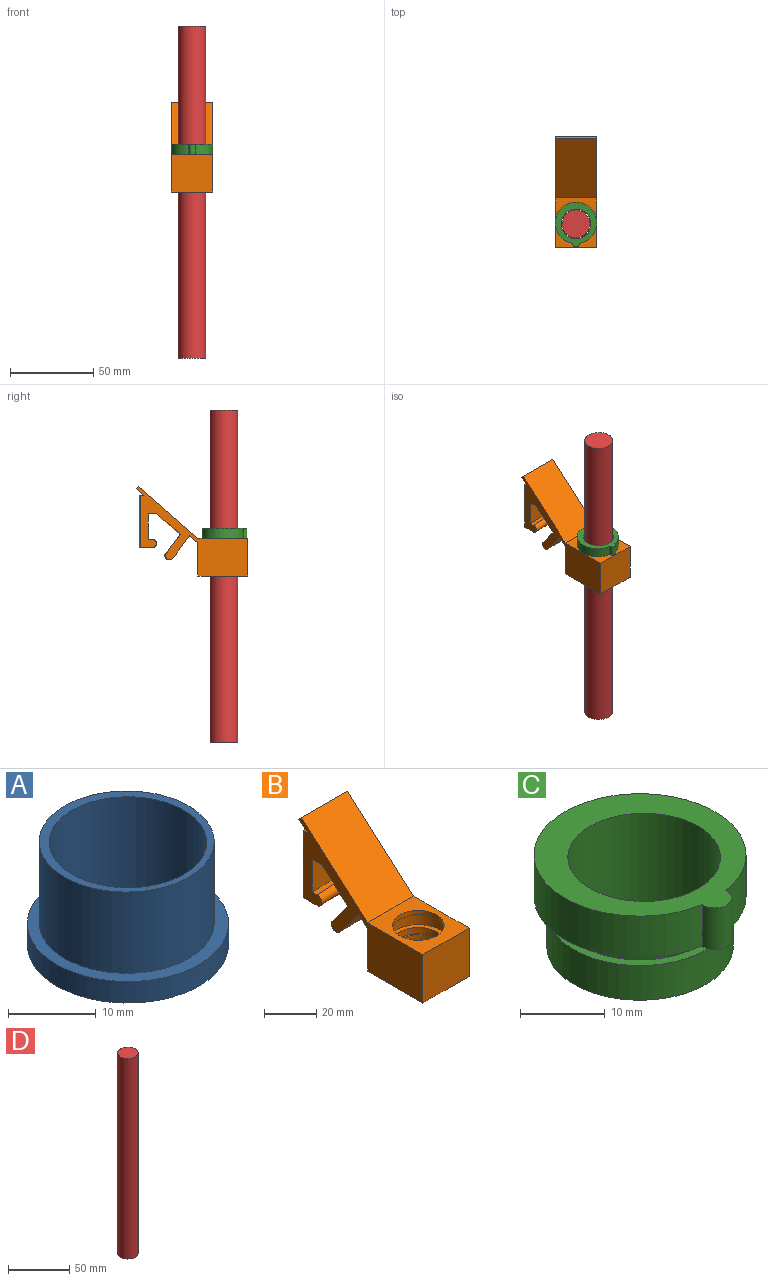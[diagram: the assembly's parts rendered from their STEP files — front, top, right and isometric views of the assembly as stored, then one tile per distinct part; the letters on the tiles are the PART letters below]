
ASSEMBLY  parts=4 mates=2
PART A: 6 faces, bbox 23x23x14.4 mm
  f0: cylinder r=10mm len=20mm, axis (0,0,1), area 713.6mm2, adj f1,f4
  f1: plane 20x20mm, normal (0,0,1), area 59.7mm2, adj f0,f5
  f2: plane 23x23mm, normal (0,0,-1), area 161mm2, adj f3,f5
  f3: cylinder r=11.5mm len=23mm, axis (0,0,1), area 216.8mm2, adj f2,f4
  f4: plane 23x23mm, normal (0,0,1), area 101.3mm2, adj f0,f3
  f5: cylinder r=9mm len=18mm, axis (0,0,-1), area 811.9mm2, adj f1,f2
PART B: 31 faces, bbox 27.2x67.2x54.1 mm
  f0: cylinder r=9.95mm len=19.9mm, axis (0,0,1), area 541.2mm2, adj f26,f28,f29
  f1: plane 67.22x54.07mm, normal (1,0,0), area 1145.6mm2, adj f3,f4,f5,f6,f7,f8,f9,f10
  f2: plane 67.22x54.07mm, normal (-1,0,0), area 1145.6mm2, adj f3,f4,f5,f6,f7,f8,f9,f10
  f3: plane 25x5.21mm, normal (0,0.66,-0.75), area 169.7mm2, adj f1,f2,f15,f20
  f4: plane 35.86x31.37mm, normal (0,-0.66,0.75), area 1191.1mm2, adj f1,f2,f5,f18
  f5: plane 25x1.51mm, normal (0,0.75,0.66), area 50mm2, adj f1,f2,f4,f16
  f6: cylinder r=186.27mm len=31.37mm, axis (0,0,-1), area 784.9mm2, adj f1,f2,f7,f17
  f7: plane 25x7.94mm, normal (0,0,-1), area 187.6mm2, adj f1,f2,f6,f8
  f8: torus R=178.77mm, axis (0,0,-1), area 196.5mm2, adj f1,f2,f7,f9
  f9: plane 25x2.94mm, normal (0,0,1), area 62.6mm2, adj f1,f2,f8,f10
  f10: cylinder r=181.27mm len=25mm, axis (0,0,-1), area 384.7mm2, adj f1,f2,f9,f11
  f11: plane 25x5.44mm, normal (0,0,-1), area 125.1mm2, adj f1,f2,f10,f12
  f12: cone r=162.09mm half-angle=48.8deg, axis (0,0,1), area 472.2mm2, adj f1,f2,f11,f13
  f13: cone r=170.54mm half-angle=36.8deg, axis (0,0,-1), area 353.1mm2, adj f1,f2,f12,f14
  f14: torus R=168.54mm, axis (0,0,-1), area 196.5mm2, adj f1,f2,f13,f15
  f15: cone r=155.31mm half-angle=36.8deg, axis (0,0,-1), area 428.8mm2, adj f1,f2,f3,f14
  f16: plane 25x4.65mm, normal (0,0.66,-0.75), area 154.3mm2, adj f1,f2,f5,f17
  f17: plane 25x2.74mm, normal (0,0,1), area 65mm2, adj f1,f2,f6,f16
  f18: plane 30x25mm, normal (0,0,1), area 439mm2, adj f1,f2,f4,f19,f22
  f19: plane 25x22.66mm, normal (0,-1,0), area 566.4mm2, adj f1,f2,f18,f21
  f20: plane 25x20mm, normal (0,1,0), area 500mm2, adj f1,f2,f3,f21
  f21: plane 30x25mm, normal (0,0,-1), area 334.5mm2, adj f1,f2,f19,f20,f30
  f22: cylinder r=9.95mm len=19.9mm, axis (0,0,1), area 125mm2, adj f18,f24
  f23: plane 23.5x23.5mm, normal (0,0,1), area 122.7mm2, adj f25,f27
  f24: plane 23.5x23.5mm, normal (0,0,-1), area 122.7mm2, adj f22,f25
  f25: cylinder r=11.75mm len=23.5mm, axis (0,0,1), area 443mm2, adj f23,f24
  f26: plane 19.9x10.3mm, normal (0,0,1), area 13.9mm2, adj f0,f27
  f27: cylinder r=9.95mm len=19.9mm, axis (0,0,1), area 187.6mm2, adj f23,f26,f28
  f28: plane 19.9x10.3mm, normal (0,0,-1), area 13.9mm2, adj f0,f27
  f29: plane 23x23mm, normal (0,0,-1), area 104.5mm2, adj f0,f30
  f30: cylinder r=11.5mm len=23mm, axis (0,0,-1), area 216.8mm2, adj f21,f29
PART C: 11 faces, bbox 25x27x14 mm
  f0: cylinder r=12.5mm len=25mm, axis (0,0,-1), area 447.2mm2, adj f7,f8,f10
  f1: cylinder r=11mm len=22mm, axis (0,0,-1), area 345.6mm2, adj f2,f3
  f2: plane 22x22mm, normal (0,0,1), area 75.3mm2, adj f1,f4
  f3: plane 22x22mm, normal (0,0,-1), area 75.3mm2, adj f1,f5
  f4: cylinder r=9.85mm len=19.7mm, axis (0,0,-1), area 136.2mm2, adj f2,f8
  f5: cylinder r=9.85mm len=19.7mm, axis (0,0,1), area 49.5mm2, adj f3,f6
  f6: plane 19.7x19.7mm, normal (0,0,-1), area 50.3mm2, adj f5,f9
  f7: plane 27x25mm, normal (0,0,1), area 242.9mm2, adj f0,f9,f10
  f8: plane 27x25mm, normal (0,0,-1), area 192.6mm2, adj f0,f4,f10
  f9: cylinder r=9mm len=18mm, axis (0,0,1), area 791.7mm2, adj f6,f7
  f10: cylinder r=2mm len=6mm, axis (0,0,1), area 39.6mm2, adj f0,f7,f8
PART D: 3 faces, bbox 16.7x16.7x200 mm
  f0: cylinder r=8.35mm len=200mm, axis (0,0,1), area 10492.9mm2, adj f1,f2
  f1: plane 16.7x16.7mm, normal (0,0,-1), area 219mm2, adj f0
  f2: plane 16.7x16.7mm, normal (0,0,1), area 219mm2, adj f0
PLACE A t=(-83.46,-113.3,-5.1)mm
PLACE B t=(-83.46,-113.3,-5.1)mm
PLACE C t=(-83.46,-113.3,-5.3)mm
PLACE D t=(-83.46,-113.3,-5.1)mm
MATE revolute C.f0 <-> B.f22  axis (0,0,-1) through (-83.46,26.7,-10.86)mm
MATE fastened D.f0 <-> A.f3  axis (0,0,1) through (-83.46,26,-33.51)mm
